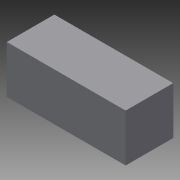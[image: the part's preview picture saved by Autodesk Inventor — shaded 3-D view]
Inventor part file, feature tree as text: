
AUTODESK INVENTOR PART (.ipt)
format: ipt  version: 2015 (Build 190159000, 159)  size: 68,608 bytes
history: native  units: mm
features: other x1, extrude x1, sketch x1
ambient origin geometry x8: Origin, YZ Plane, XZ Plane, XY Plane, X Axis, Y Axis, Z Axis, Center Point
bodies: Body1 (feature_tree)
feature tree (3):
  other  "ソリッド1"
  extrude  "押し出し1"  Depth=75.0mm
  sketch  "スケッチ1"
